FCSTD DOCUMENT  (FreeCAD 2023.521R14555 (Git shallow))
Label: Joint
License: All rights reserved
LicenseURL: http://en.wikipedia.org/wiki/All_rights_reserved
objects: App::Link×15, App::DocumentObjectGroup×3, PartDesign::CoordinateSystem×1, App::FeaturePython×1, App::Part×1
note: 1 computed .brp shape members not serialized (recipe doc carries the construction recipe); baked Part::Feature solids carry a one-line shape summary decoded from their .brp
EXTERNAL_REF file=parts/spark_encoder.FCStd obj=Home
EXTERNAL_REF file=parts/spark_encoder.FCStd obj=Part
EXTERNAL_REF file=prefab/Bearing_6x16x4.FCStd obj=Local_CS
EXTERNAL_REF file=parts/spark_encoder.FCStd obj=Local_CS
EXTERNAL_REF file=prefab/Bearing_6x16x4.FCStd obj=Part
EXTERNAL_REF file=parts/spark_encoder.FCStd obj=Local_CS003
EXTERNAL_REF file=prefab/Shaft.FCStd obj=LCS_1
EXTERNAL_REF file=prefab/Shaft.FCStd obj=Part
EXTERNAL_REF file=prefab/Bearing_6x16x4.FCStd obj=Local_CS001
EXTERNAL_REF file=prefab/Collar_6x19x9.FCStd obj=LCS_1
EXTERNAL_REF file=prefab/Collar_6x19x9.FCStd obj=Part
EXTERNAL_REF file=parts/spark_mag_holder.FCStd obj=LCS_1
EXTERNAL_REF file=parts/spark_mag_holder.FCStd obj=Mag_holder
EXTERNAL_REF file=prefab/Magnet.FCStd obj=LCS_1
EXTERNAL_REF file=parts/spark_mag_holder.FCStd obj=LCS_2
EXTERNAL_REF file=prefab/Magnet.FCStd obj=Body
EXTERNAL_REF file=prefab/Screw.FCStd obj=Base
EXTERNAL_REF file=parts/spark_encoder.FCStd obj=Local_CS006
EXTERNAL_REF file=prefab/Screw.FCStd obj=Screw
EXTERNAL_REF file=parts/spark_encoder.FCStd obj=Local_CS007
EXTERNAL_REF file=parts/spark_encoder.FCStd obj=Local_CS008
EXTERNAL_REF file=parts/spark_encoder.FCStd obj=Local_CS009
EXTERNAL_REF file=parts/spark_encoder.FCStd obj=Local_CS010
EXTERNAL_REF file=parts/spark_encoder.FCStd obj=Local_CS011
EXTERNAL_REF file=prefab/Hub_6.FCStd obj=Face
EXTERNAL_REF file=prefab/Hub_6.FCStd obj=Part
EXTERNAL_REF file=prefab/Encoder_PCB.FCStd obj=LCS_1
EXTERNAL_REF file=parts/spark_encoder.FCStd obj=Local_CS005
EXTERNAL_REF file=prefab/Encoder_PCB.FCStd obj=Encoder

FEATURE [App::DocumentObjectGroup] Parts
  ClaimAllChildren = true
  ExportMode = 1
  TreeRank = 0
  _GroupVersion = 1
FEATURE [PartDesign::CoordinateSystem] LCS_Origin
  AttacherType = Attacher::AttachEngine3D
  AttachmentSupport = -> [X_Axis]
  InvalidShape = false
  MapMode = 2
  Support = -> [X_Axis]
  TreeRank = 0
  ValidateShape = false
FEATURE [App::DocumentObjectGroup] Constraints
  ClaimAllChildren = true
  ExportMode = 1
  TreeRank = 0
  _GroupVersion = 1
FEATURE [App::FeaturePython] Variables  # WARN: FeaturePython — macro-defined, semantics opaque (R4)
  TreeRank = 0
  Type = App::PropertyContainer
FEATURE [App::DocumentObjectGroup] Configurations
  ClaimAllChildren = true
  ExportMode = 1
  TreeRank = 0
  _GroupVersion = 1
FEATURE [App::Link] Encoder  label="Encoder(Encoder)"
  AttachedBy = #Home
  AttachedTo = Parent Assembly#LCS_Origin
  AttachmentOffset = pos=(0,0,0) rot=(-0.57735,0.57735,-0.57735;4.18879rad)
  AutoLinkLabel = true
  AutoPlacement = true
  LinkPlacement = pos=(0,0,0) rot=(0,0,1;4.71239rad)
  LinkedObject = -> <external parts/spark_encoder.FCStd>#Part
  Placement = pos=(0,0,0) rot=(0,0,1;4.71239rad)
  SolverId = Asm4EE
  SyncGroupVisibility = false
  TreeRank = 1
  _LinkVersion = 1
  expr: Placement = LCS_Origin.Placement * AttachmentOffset * spark_encoder#Home.Placement ^ (-1)
FEATURE [App::Link] Bearing  label="Bearing(Bearing)"
  AttachedBy = #Local_CS
  AttachedTo = Encoder#Local_CS
  AutoLinkLabel = true
  AutoPlacement = true
  LinkPlacement = pos=(5.3e-15,-20,1.14e-14) rot=(0.707107,0,0.707107;3.14159rad)
  LinkedObject = -> <external prefab/Bearing_6x16x4.FCStd>#Part
  Placement = pos=(5.3e-15,-20,1.14e-14) rot=(0.707107,0,0.707107;3.14159rad)
  SolverId = Asm4EE
  SyncGroupVisibility = false
  TreeRank = 2
  _LinkVersion = 1
  expr: Placement = Encoder.Placement * spark_encoder#Local_CS.Placement * AttachmentOffset * Bearing_6x16x4#Local_CS.Placement ^ (-1)
FEATURE [App::Link] Bearing001  label="Bearing"
  AttachedBy = #Local_CS
  AttachedTo = Encoder#Local_CS003
  AutoLinkLabel = true
  AutoPlacement = true
  LinkPlacement = pos=(1.27e-14,-53,3.29e-14) rot=(0,1,0;1.5708rad)
  LinkedObject = -> <external prefab/Bearing_6x16x4.FCStd>#Part
  Placement = pos=(1.27e-14,-53,3.29e-14) rot=(0,1,0;1.5708rad)
  SolverId = Asm4EE
  SyncGroupVisibility = false
  TreeRank = 3
  _LinkVersion = 1
  expr: Placement = Encoder.Placement * spark_encoder#Local_CS003.Placement * AttachmentOffset * Bearing_6x16x4#Local_CS.Placement ^ (-1)
FEATURE [App::Link] Shaft  label="Shaft(Shaft)"
  AttachedBy = #LCS_1
  AttachedTo = Encoder#Home
  AttachmentOffset = pos=(0,0,6) rot=(0,0,1;0rad)
  AutoLinkLabel = true
  AutoPlacement = true
  LinkPlacement = pos=(1.3e-15,-6,2.7e-15) rot=(0,0,1;0rad)
  LinkedObject = -> <external prefab/Shaft.FCStd>#Part
  Placement = pos=(1.3e-15,-6,2.7e-15) rot=(0,0,1;0rad)
  SolverId = Asm4EE
  SyncGroupVisibility = false
  TreeRank = 4
  _LinkVersion = 1
  expr: Placement = Encoder.Placement * spark_encoder#Home.Placement * AttachmentOffset * Shaft#LCS_1.Placement ^ (-1)
FEATURE [App::Link] Collar  label="Collar(Collar)"
  AttachedBy = #LCS_1
  AttachedTo = Bearing#Local_CS001
  AutoLinkLabel = true
  AutoPlacement = true
  LinkPlacement = pos=(-24.7535,-15.5204,25.1307) rot=(0.6,0,0.8;3.14159rad)
  LinkedObject = -> <external prefab/Collar_6x19x9.FCStd>#Part
  Placement = pos=(-24.7535,-15.5204,25.1307) rot=(0.6,0,0.8;3.14159rad)
  SolverId = Asm4EE
  SyncGroupVisibility = false
  TreeRank = 5
  _LinkVersion = 1
  expr: Placement = Bearing.Placement * Bearing_6x16x4#Local_CS001.Placement * AttachmentOffset * Collar_6x19x9#LCS_1.Placement ^ (-1)
FEATURE [App::Link] Mag_holder  label="Mag_holder(Mag_holder)"
  AttachedBy = #LCS_1
  AttachedTo = Shaft#LCS_1
  AutoLinkLabel = true
  AutoPlacement = true
  LinkPlacement = pos=(2.4e-15,-10,3.3e-15) rot=(-0.57735,0.57735,0.57735;4.18879rad)
  LinkedObject = -> <external parts/spark_mag_holder.FCStd>#Mag_holder
  Placement = pos=(2.4e-15,-10,3.3e-15) rot=(-0.57735,0.57735,0.57735;4.18879rad)
  SolverId = Asm4EE
  SyncGroupVisibility = false
  TreeRank = 6
  _LinkVersion = 1
  expr: Placement = Shaft.Placement * Shaft#LCS_1.Placement * AttachmentOffset * spark_mag_holder#LCS_1.Placement ^ (-1)
FEATURE [App::Link] Magnet  label="Magnet(Magnet)"
  AttachedBy = #LCS_1
  AttachedTo = Mag_holder#LCS_2
  AttachmentOffset = pos=(0,0,0) rot=(0,1,0;3.14159rad)
  AutoLinkLabel = true
  AutoPlacement = true
  LinkPlacement = pos=(5e-16,-1.325,1.5e-15) rot=(-0.57735,0.57735,0.57735;4.18879rad)
  LinkedObject = -> <external prefab/Magnet.FCStd>#Body
  Placement = pos=(5e-16,-1.325,1.5e-15) rot=(-0.57735,0.57735,0.57735;4.18879rad)
  SolverId = Asm4EE
  SyncGroupVisibility = false
  TreeRank = 7
  _LinkVersion = 1
  expr: Placement = Mag_holder.Placement * spark_mag_holder#LCS_2.Placement * AttachmentOffset * Magnet#LCS_1.Placement ^ (-1)
FEATURE [App::Link] Screw  label="Screw(Screw)"
  AttachedBy = #Base
  AttachedTo = Encoder#Local_CS006
  AutoLinkLabel = true
  AutoPlacement = true
  LinkPlacement = pos=(-8,-5,-18.0312) rot=(1,0,0;3.14159rad)
  LinkedObject = -> <external prefab/Screw.FCStd>#Screw
  Placement = pos=(-8,-5,-18.0312) rot=(1,0,0;3.14159rad)
  SolverId = Asm4EE
  SyncGroupVisibility = false
  TreeRank = 8
  _LinkVersion = 1
  expr: Placement = Encoder.Placement * spark_encoder#Local_CS006.Placement * AttachmentOffset * Screw#Base.Placement ^ (-1)
FEATURE [App::Link] Screw_Screw_  label="Screw(Screw)001"
  AttachedBy = #Base
  AttachedTo = Encoder#Local_CS007
  AutoLinkLabel = true
  AutoPlacement = true
  LinkPlacement = pos=(-8,-25,-18.0312) rot=(1,0,0;3.14159rad)
  LinkedObject = -> <external prefab/Screw.FCStd>#Screw
  Placement = pos=(-8,-25,-18.0312) rot=(1,0,0;3.14159rad)
  SolverId = Asm4EE
  SyncGroupVisibility = false
  TreeRank = 9
  _LinkVersion = 1
  expr: Placement = Encoder.Placement * spark_encoder#Local_CS007.Placement * AttachmentOffset * Screw#Base.Placement ^ (-1)
FEATURE [App::Link] Screw_Screw__1  label="Screw(Screw)_1"
  AttachedBy = #Base
  AttachedTo = Encoder#Local_CS008
  AutoLinkLabel = true
  AutoPlacement = true
  LinkPlacement = pos=(-8,-45,-18.0312) rot=(0.70711,-0.707103,0;3.14159rad)
  LinkedObject = -> <external prefab/Screw.FCStd>#Screw
  Placement = pos=(-8,-45,-18.0312) rot=(0.70711,-0.707103,0;3.14159rad)
  SolverId = Asm4EE
  SyncGroupVisibility = false
  TreeRank = 10
  _LinkVersion = 1
  expr: Placement = Encoder.Placement * spark_encoder#Local_CS008.Placement * AttachmentOffset * Screw#Base.Placement ^ (-1)
FEATURE [App::Link] Screw_Screw__1001  label="Screw(Screw)_002"
  AttachedBy = #Base
  AttachedTo = Encoder#Local_CS009
  AutoLinkLabel = true
  AutoPlacement = true
  LinkPlacement = pos=(8,-5,-18.0312) rot=(1,0,0;3.14159rad)
  LinkedObject = -> <external prefab/Screw.FCStd>#Screw
  Placement = pos=(8,-5,-18.0312) rot=(1,0,0;3.14159rad)
  SolverId = Asm4EE
  SyncGroupVisibility = false
  TreeRank = 11
  _LinkVersion = 1
  expr: Placement = Encoder.Placement * spark_encoder#Local_CS009.Placement * AttachmentOffset * Screw#Base.Placement ^ (-1)
FEATURE [App::Link] Screw_Screw__1002  label="Screw(Screw)_003"
  AttachedBy = #Base
  AttachedTo = Encoder#Local_CS010
  AutoLinkLabel = true
  AutoPlacement = true
  LinkPlacement = pos=(8,-25,-18.0312) rot=(1,0,0;3.14159rad)
  LinkedObject = -> <external prefab/Screw.FCStd>#Screw
  Placement = pos=(8,-25,-18.0312) rot=(1,0,0;3.14159rad)
  SolverId = Asm4EE
  SyncGroupVisibility = false
  TreeRank = 12
  _LinkVersion = 1
  expr: Placement = Encoder.Placement * spark_encoder#Local_CS010.Placement * AttachmentOffset * Screw#Base.Placement ^ (-1)
FEATURE [App::Link] Screw_Screw__1003  label="Screw(Screw)_004"
  AttachedBy = #Base
  AttachedTo = Encoder#Local_CS011
  AutoLinkLabel = true
  AutoPlacement = true
  LinkPlacement = pos=(8,-45,-18.0312) rot=(1,0,0;3.14159rad)
  LinkedObject = -> <external prefab/Screw.FCStd>#Screw
  Placement = pos=(8,-45,-18.0312) rot=(1,0,0;3.14159rad)
  SolverId = Asm4EE
  SyncGroupVisibility = false
  TreeRank = 13
  _LinkVersion = 1
  expr: Placement = Encoder.Placement * spark_encoder#Local_CS011.Placement * AttachmentOffset * Screw#Base.Placement ^ (-1)
FEATURE [App::Link] Hub  label="Hub(Hub)"
  AttachedBy = #Face
  AttachedTo = Bearing001#Local_CS001
  AutoLinkLabel = true
  AutoPlacement = true
  LinkPlacement = pos=(-4.97356,-60.3025,-1.29993) rot=(0,-0.707107,-0.707107;3.14159rad)
  LinkedObject = -> <external prefab/Hub_6.FCStd>#Part
  Placement = pos=(-4.97356,-60.3025,-1.29993) rot=(0,-0.707107,-0.707107;3.14159rad)
  SolverId = Asm4EE
  SyncGroupVisibility = false
  TreeRank = 14
  _LinkVersion = 1
  expr: Placement = Bearing001.Placement * Bearing_6x16x4#Local_CS001.Placement * AttachmentOffset * Hub_6#Face.Placement ^ (-1)
FEATURE [App::Link] Encoder_PCB  label="Encoder_PCB(Encoder_PCB)"
  AttachedBy = #LCS_1
  AttachedTo = Encoder#Local_CS005
  AttachmentOffset = pos=(0,0,0) rot=(0,0,1;4.71239rad)
  AutoLinkLabel = true
  AutoPlacement = true
  LinkPlacement = pos=(-3.11755,1.6,5.97034) rot=(0.999998,0.001249,-0.001249;1.5708rad)
  LinkedObject = -> <external prefab/Encoder_PCB.FCStd>#Encoder
  Placement = pos=(-3.11755,1.6,5.97034) rot=(0.999998,0.001249,-0.001249;1.5708rad)
  SolverId = Asm4EE
  SyncGroupVisibility = false
  TreeRank = 15
  _LinkVersion = 1
  expr: Placement = Encoder.Placement * spark_encoder#Local_CS005.Placement * AttachmentOffset * Encoder_PCB#LCS_1.Placement ^ (-1)
FEATURE [App::Part] Assembly
  AssemblyType = Part::Link
  ClaimAllChildren = false
  ExportMode = 1
  Group = -> [LCS_Origin,Constraints,Variables,Configurations,Encoder,Bearing,Bearing001,Shaft,Collar,Mag_holder,Magnet,Screw,Screw_Screw_,Screw_Screw__1,Screw_Screw__1001,Screw_Screw__1002,Screw_Screw__1003,Hub,Encoder_PCB]
  Origin = -> Origin
  TreeRank = 0
  Type = Assembly
  _ExportChildren = -> [LCS_Origin,Constraints,Variables,Configurations,Encoder,Bearing,Bearing001,Shaft,Collar,Mag_holder,Magnet,Screw,Screw_Screw_,Screw_Screw__1,Screw_Screw__1001,Screw_Screw__1002,Screw_Screw__1003,Hub,Encoder_PCB]
  _GroupVersion = 1

RESOLVED EXTERNAL PARTS (link-assembly join: the EXTERNAL_REF files above that resolve inside this repo's crawl, each included once):
---- part prefab/Magnet.FCStd = doc fcstd_837fa72243f5 ----
FCSTD DOCUMENT  (FreeCAD 2023.521R14555 (Git shallow))
Label: Magnet
License: All rights reserved
LicenseURL: http://en.wikipedia.org/wiki/All_rights_reserved
objects: Sketcher::SketchObject×1, PartDesign::Pad×1, PartDesign::CoordinateSystem×1, PartDesign::Body×1
note: 7 computed .brp shape members not serialized (recipe doc carries the construction recipe); baked Part::Feature solids carry a one-line shape summary decoded from their .brp

FEATURE [Sketcher::SketchObject] Sketch
  ArcFitTolerance = 0
  AttachmentSupport = -> [YZ_Plane]
  ExternalBSplineMaxDegree = 0
  ExternalBSplineTolerance = 0
  FullyConstrained = true
  InternalTolerance = 1e-06
  InvalidShape = false
  MakeInternals = false
  MapMode = 5
  Placement = pos=(0,0,0) rot=(0.57735,0.57735,0.57735;2.0944rad)
  Support = -> [YZ_Plane]
  TreeRank = 0
  ValidateShape = false
  sketch-geometry (1):
    g0: Circle CenterX=0 CenterY=0 CenterZ=0 NormalX=0 NormalY=0 NormalZ=1 AngleXU=0 Radius=3.96875
  constraints (2):
    c: Coincident(g0,g-1)
    c: Diameter(g0) = 7.9375
FEATURE [PartDesign::Pad] Pad
  AddSubType = 0
  AutoTaperInnerAngle = true
  CheckUpToFaceLimits = true
  ClaimChildren = false
  Direction = (1,-2e-16,3e-16)
  Fit = 0
  FitJoin = 0
  InnerFit = 0
  InnerFitJoin = 0
  InvalidShape = false
  Length = 3.175
  Length2 = 10
  NewSolid = false
  Profile = -> Sketch
  ReferenceAxis = -> Sketch [N_Axis]
  Suppress = false
  TaperInnerAngle = 0
  TaperInnerAngleRev = 0
  TreeRank = 0
  Type = 0
  ValidateShape = true
  _ProfileBasedVersion = 0
FEATURE [PartDesign::CoordinateSystem] LCS_1
  AttacherType = Attacher::AttachEngine3D
  AttachmentSupport = -> [Pad]
  InvalidShape = false
  MapMode = 45
  Placement = pos=(3.175,-1.1e-15,1e-15) rot=(0.57735,0.57735,0.57735;2.0944rad)
  Support = -> [Pad]
  TreeRank = 0
  ValidateShape = false
FEATURE [PartDesign::Body] Body  label="Magnet"
  AutoGroupSolids = false
  ClaimAllChildren = false
  ExportMode = 0
  Group = -> [Sketch,Pad,LCS_1]
  InvalidShape = false
  Origin = -> Origin
  Tip = -> Pad
  TreeRank = 0
  ValidateShape = false
  _ExportChildren = -> [Pad,LCS_1]
  _GroupVersion = 1
---- part prefab/Shaft.FCStd = doc fcstd_3dcb7cfc0477 ----
FCSTD DOCUMENT  (FreeCAD 2023.521R14555 (Git shallow))
Label: Shaft
License: All rights reserved
LicenseURL: http://en.wikipedia.org/wiki/All_rights_reserved
objects: PartDesign::CoordinateSystem×2, Sketcher::SketchObject×1, PartDesign::Pad×1, PartDesign::Body×1, App::Part×1
note: 8 computed .brp shape members not serialized (recipe doc carries the construction recipe); baked Part::Feature solids carry a one-line shape summary decoded from their .brp

FEATURE [Sketcher::SketchObject] Sketch
  ArcFitTolerance = 0
  AttachmentSupport = -> [XZ_Plane]
  ExternalBSplineMaxDegree = 0
  ExternalBSplineTolerance = 0
  FullyConstrained = true
  InternalTolerance = 1e-06
  InvalidShape = false
  MakeInternals = false
  MapMode = 5
  Placement = pos=(0,0,0) rot=(1,0,0;1.5708rad)
  Support = -> [XZ_Plane]
  TreeRank = 0
  ValidateShape = false
  sketch-geometry (1):
    g0: Circle CenterX=0 CenterY=0 CenterZ=0 NormalX=0 NormalY=0 NormalZ=1 AngleXU=0 Radius=3
  constraints (2):
    c: Coincident(g0,g-1)
    c: Diameter(g0) = 6
FEATURE [PartDesign::Pad] Pad
  AddSubType = 0
  AutoTaperInnerAngle = true
  CheckUpToFaceLimits = true
  ClaimChildren = false
  Direction = (0,-1,-2e-16)
  Fit = 0
  FitJoin = 0
  InnerFit = 0
  InnerFitJoin = 0
  InvalidShape = false
  Length = 70
  Length2 = 10
  NewSolid = false
  Profile = -> Sketch
  ReferenceAxis = -> Sketch [N_Axis]
  Suppress = false
  TaperInnerAngle = 0
  TaperInnerAngleRev = 0
  TreeRank = 0
  Type = 0
  ValidateShape = true
  _ProfileBasedVersion = 0
FEATURE [PartDesign::Body] Shaft  label="Shaft001"
  AutoGroupSolids = false
  ClaimAllChildren = false
  ExportMode = 0
  Group = -> [Sketch,Pad]
  InvalidShape = false
  Origin = -> Origin
  Tip = -> Pad
  TreeRank = 0
  ValidateShape = false
  _ExportChildren = -> [Pad]
  _GroupVersion = 1
FEATURE [PartDesign::CoordinateSystem] LCS_1
  AttacherType = Attacher::AttachEngine3D
  AttachmentSupport = -> [Pad]
  InvalidShape = false
  MapMode = 11
  Placement = pos=(0,0,0) rot=(0.57735,-0.57735,0.57735;2.0944rad)
  Support = -> [Pad]
  TreeRank = 0
  ValidateShape = false
FEATURE [PartDesign::CoordinateSystem] End
  AttacherType = Attacher::AttachEngine3D
  AttachmentSupport = -> [Pad]
  InvalidShape = false
  MapMode = 11
  Placement = pos=(0,-70,-1.55e-14) rot=(0.57735,-0.57735,0.57735;2.0944rad)
  Support = -> [Pad]
  TreeRank = 0
  ValidateShape = false
FEATURE [App::Part] Part  label="Shaft"
  ClaimAllChildren = false
  ExportMode = 1
  Group = -> [Shaft,LCS_1,End]
  Origin = -> Origin001
  TreeRank = 0
  _ExportChildren = -> [Shaft,LCS_1,End]
  _GroupVersion = 1
